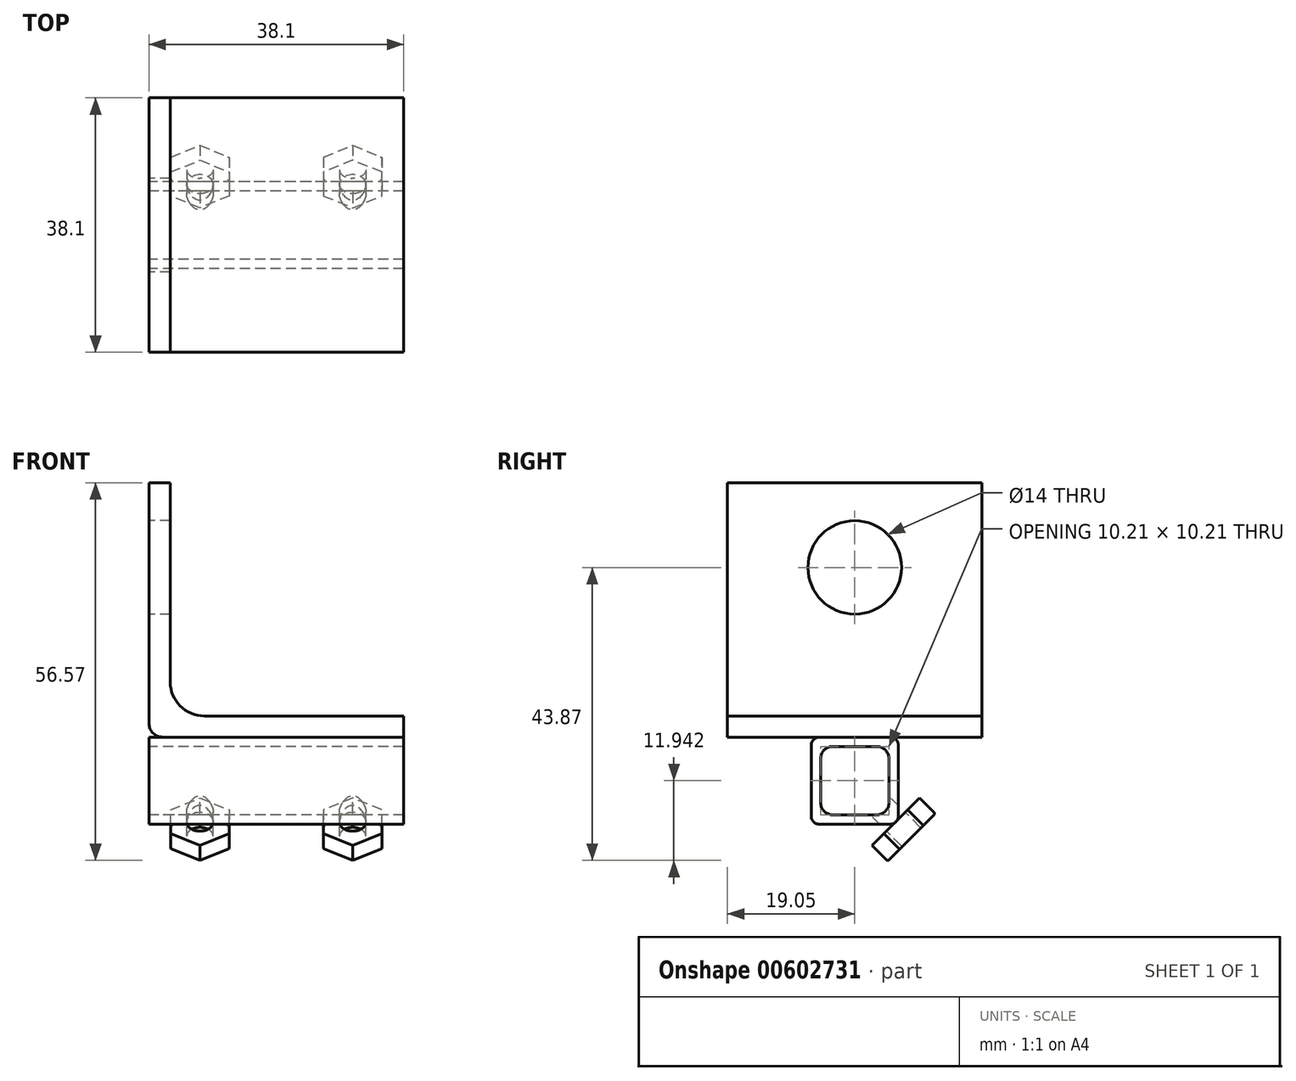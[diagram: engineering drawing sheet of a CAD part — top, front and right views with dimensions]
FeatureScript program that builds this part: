
annotation { "Feature Type Name" : "Feature", "Feature Type Description" : "" }
export const myFeature = defineFeature(function(context is Context, id is Id, definition is map)
    precondition{}
    {
        {
            var Q0;
            Q0=qCreatedBy(makeId("Front.planeOp"),FACE);
            var sketch = newSketch(context, id + "F0", { "sketchPlane" : qUnion([Q0])});
            skLineSegment(sketch, "E0", {"start": v(0, 38.1) * mm, "end": v(0, 0) * mm});
            skLineSegment(sketch, "E1", {"start": v(0, 0) * mm, "end": v(38.1, 0) * mm});
            skLineSegment(sketch, "E2", {"start": v(38.1, 0) * mm, "end": v(38.1, 3.17) * mm});
            skLineSegment(sketch, "E3", {"start": v(38.1, 3.17) * mm, "end": v(3.17, 3.17) * mm});
            skLineSegment(sketch, "E4", {"start": v(3.18, 3.17) * mm, "end": v(3.18, 38.1) * mm});
            skLineSegment(sketch, "E5", {"start": v(3.17, 38.1) * mm, "end": v(0, 38.1) * mm});
            skSolve(sketch);
        }
        {
            var Q0;
            Q0=makeQuery(id+"F0.imprint","IMPRINT",FACE,{"disambiguationData":[TD([[makeQuery(id+"F0.imprint","IMPRINT",EDGE,{"derivedFrom":sQuery(id+"F0.wireOp",EDGE,"E0")}),1.0]])]});
            extrude(context, id + "F1", {"entities" : qUnion([Q0]), "depth" : 38.1 * mm, "offsetDistance" : 25.4 * mm});
        }
        {
            var Q0;
            Q0=makeQuery(id+"F1.opExtrude","SWEPT_FACE",FACE,{"disambiguationData":[OSD([sQuery(id+"F0.wireOp",EDGE,"E0")])]});
            var sketch = newSketch(context, id + "F2", { "sketchPlane" : qUnion([Q0])});
            skCircle(sketch, "E6", {"center": v(19.05, 25.4) * mm, "radius": 7 * mm});
            skLineSegment(sketch, "E7", {"start": v(19.05, 38.1) * mm, "end": v(19.05, 25.4) * mm, "construction": true});
            skSolve(sketch);
        }
        {
            var Q0;
            Q0 = qSketchRegion(id + "F2", true);
            extrude(context, id + "F3", {"entities" : qUnion([Q0]), "operationType" : NewBodyOperationType.REMOVE, "endBound" : BoundingType.THROUGH_ALL, "oppositeDirection" : true, "depth" : 25.4 * mm, "offsetDistance" : 25.4 * mm});
        }
        {
            var Q0;
            Q0=makeQuery(id+"F1.opExtrude","SWEPT_EDGE",EDGE,{"disambiguationData":[OSD([sQuery(id+"F0.wireOp",EDGE,"E0"),sQuery(id+"F0.wireOp",EDGE,"E1")])]});
            fillet(context, id + "F4", {"entities" : qUnion([Q0]), "radius" : 2.03 * mm, "tangentPropagation" : true, "allowEdgeOverflow" : false});
        }
        {
            var Q0;
            Q0=makeQuery(id+"F1.opExtrude","SWEPT_EDGE",EDGE,{"disambiguationData":[OSD([sQuery(id+"F0.wireOp",EDGE,"E3"),sQuery(id+"F0.wireOp",EDGE,"E4")])]});
            fillet(context, id + "F5", {"entities" : qUnion([Q0]), "radius" : 5.08 * mm, "tangentPropagation" : true, "allowEdgeOverflow" : false});
        }
        {
            var Q0;
            Q0=makeQuery(id+"F1.opExtrude","SWEPT_FACE",FACE,{"disambiguationData":[OSD([sQuery(id+"F0.wireOp",EDGE,"E0")])]});
            var sketch = newSketch(context, id + "F6", { "sketchPlane" : qUnion([Q0])});
            skLineSegment(sketch, "E8.bottom", {"start": v(12.52, -13.06) * mm, "end": v(25.58, -13.06) * mm});
            skLineSegment(sketch, "E8.top", {"start": v(12.52, 0) * mm, "end": v(25.58, 0) * mm});
            skLineSegment(sketch, "E8.left", {"start": v(12.52, -13.06) * mm, "end": v(12.52, 0) * mm});
            skLineSegment(sketch, "E8.right", {"start": v(25.58, -13.06) * mm, "end": v(25.58, 0) * mm});
            skPoint(sketch, "E9", {"position": v(19.05, 0) * mm});
            skSolve(sketch);
        }
        {
            var Q0;
            Q0 = qSketchRegion(id + "F6", true);
            var Q1;
            Q1=makeQuery(id+"F1.opExtrude","SWEPT_FACE",FACE,{"disambiguationData":[OSD([sQuery(id+"F0.wireOp",EDGE,"E2")])]});
            extrude(context, id + "F7", {"entities" : qUnion([Q0]), "endBound" : BoundingType.UP_TO_SURFACE, "oppositeDirection" : true, "depth" : 25.4 * mm, "endBoundEntityFace" : qUnion([Q1]), "offsetDistance" : 25.4 * mm});
        }
        {
            var Q0;
            Q0=makeQuery(id+"F7.opExtrude","CAP_FACE",FACE,{"disambiguationData":[OSD([sQuery(id+"F6.wireOp",EDGE,"E8.bottom"),sQuery(id+"F6.wireOp",EDGE,"E8.top"),sQuery(id+"F6.wireOp",EDGE,"E8.left"),sQuery(id+"F6.wireOp",EDGE,"E8.right")])],"isStart":false});
            var Q1;
            Q1=makeQuery(id+"F7.opExtrude","CAP_FACE",FACE,{"disambiguationData":[OSD([sQuery(id+"F6.wireOp",EDGE,"E8.bottom"),sQuery(id+"F6.wireOp",EDGE,"E8.top"),sQuery(id+"F6.wireOp",EDGE,"E8.left"),sQuery(id+"F6.wireOp",EDGE,"E8.right")])],"isStart":true});
            shell(context, id + "F8", {"entities" : qUnion([Q0, Q1]), "thickness" : 1.42 * mm});
        }
        {
            var Q0;
            Q0=makeQuery(id+"F7.opExtrude","SWEPT_EDGE",EDGE,{"disambiguationData":[OSD([sQuery(id+"F6.wireOp",EDGE,"E8.bottom"),sQuery(id+"F6.wireOp",EDGE,"E8.right")])]});
            var Q1;
            Q1=makeQuery(id+"F7.opExtrude","SWEPT_EDGE",EDGE,{"disambiguationData":[OSD([sQuery(id+"F6.wireOp",EDGE,"E8.top"),sQuery(id+"F6.wireOp",EDGE,"E8.right")])]});
            var Q2;
            Q2=makeQuery(id+"F7.opExtrude","SWEPT_EDGE",EDGE,{"disambiguationData":[OSD([sQuery(id+"F6.wireOp",EDGE,"E8.bottom"),sQuery(id+"F6.wireOp",EDGE,"E8.left")])]});
            var Q3;
            Q3=makeQuery(id+"F7.opExtrude","SWEPT_EDGE",EDGE,{"disambiguationData":[OSD([sQuery(id+"F6.wireOp",EDGE,"E8.top"),sQuery(id+"F6.wireOp",EDGE,"E8.left")])]});
            fillet(context, id + "F9", {"entities" : qUnion([Q0, Q1, Q2, Q3]), "radius" : 1.27 * mm, "tangentPropagation" : true, "allowEdgeOverflow" : false});
        }
        {
            var Q0;
            Q0=makeQuery(id+"F8.opShell","OFFSET_EDGE",EDGE,{"disambiguationData":[OSD([sQuery(id+"F6.wireOp",EDGE,"E8.bottom"),sQuery(id+"F6.wireOp",EDGE,"E8.right")])]});
            var Q1;
            Q1=makeQuery(id+"F8.opShell","OFFSET_EDGE",EDGE,{"disambiguationData":[OSD([sQuery(id+"F6.wireOp",EDGE,"E8.top"),sQuery(id+"F6.wireOp",EDGE,"E8.right")])]});
            var Q2;
            Q2=makeQuery(id+"F8.opShell","OFFSET_EDGE",EDGE,{"disambiguationData":[OSD([sQuery(id+"F6.wireOp",EDGE,"E8.top"),sQuery(id+"F6.wireOp",EDGE,"E8.left")])]});
            var Q3;
            Q3=makeQuery(id+"F8.opShell","OFFSET_EDGE",EDGE,{"disambiguationData":[OSD([sQuery(id+"F6.wireOp",EDGE,"E8.bottom"),sQuery(id+"F6.wireOp",EDGE,"E8.left")])]});
            fillet(context, id + "F10", {"entities" : qUnion([Q0, Q1, Q2, Q3]), "radius" : 1.78 * mm, "tangentPropagation" : true, "allowEdgeOverflow" : false});
        }
        {
            var Q0;
            Q0=makeQuery(id+"F7.opExtrude","SWEPT_FACE",FACE,{"disambiguationData":[OSD([sQuery(id+"F6.wireOp",EDGE,"E8.bottom")])]});
            var Q1;
            {var subQ0=sQuery(id+"F6.wireOp",EDGE,"E8.bottom");Q1=makeQuery(id+"F9.opFillet","BLEND_EDGE",EDGE,{"blendedFrom":[makeQuery(id+"F7.opExtrude","SWEPT_EDGE",EDGE,{"disambiguationData":[OSD([subQ0,sQuery(id+"F6.wireOp",EDGE,"E8.right")])]}),makeQuery(id+"F7.opExtrude","SWEPT_FACE",FACE,{"disambiguationData":[OSD([subQ0])]})],"blendedInto":[makeQuery(id+"F7.opExtrude","SWEPT_FACE",FACE,{"disambiguationData":[OSD([subQ0])]})]});}
            cPlane(context, id + "F11", {"entities" : qUnion([Q0, Q1]), "cplaneType" : CPlaneType.LINE_ANGLE, "offset" : 25.4 * mm, "angle" : 45 * degree, "oppositeDirection" : true, "width" : 152.4 * mm, "height" : 152.4 * mm});
        }
        {
            var Q0;
            Q0=qCreatedBy(id+"F11.planeOp",FACE);
            var sketch = newSketch(context, id + "F12", { "sketchPlane" : qUnion([Q0])});
            skCircle(sketch, "E10", {"center": v(30.48, -18.09) * mm, "radius": 1.98 * mm});
            skLineSegment(sketch, "E11", {"start": v(30.48, -18.09) * mm, "end": v(38.1, -18.09) * mm, "construction": true});
            skLineSegment(sketch, "E12", {"start": v(19.05, -18.98) * mm, "end": v(19.05, -28.6) * mm, "construction": true});
            skCircle(sketch, "E13.MirrorC", {"center": v(7.62, -18.09) * mm, "radius": 1.98 * mm});
            skSolve(sketch);
        }
        {
            var Q0;
            Q0 = qSketchRegion(id + "F12", true);
            extrude(context, id + "F13", {"entities" : qUnion([Q0]), "operationType" : NewBodyOperationType.REMOVE, "endBound" : BoundingType.THROUGH_ALL, "oppositeDirection" : true, "depth" : 25.4 * mm, "offsetDistance" : 25.4 * mm});
        }
        {
            var Q0;
            {var subQ0=sQuery(id+"F6.wireOp",EDGE,"E8.left");var subQ1=sQuery(id+"F6.wireOp",EDGE,"E8.bottom");Q0=makeQuery(id+"F9.opFillet","BLEND_EDGE",EDGE,{"blendedFrom":[makeQuery(id+"F7.opExtrude","SWEPT_EDGE",EDGE,{"disambiguationData":[OSD([subQ1,subQ0])]}),makeQuery(id+"F7.opExtrude","CAP_FACE",FACE,{"disambiguationData":[OSD([subQ1,sQuery(id+"F6.wireOp",EDGE,"E8.top"),subQ0,sQuery(id+"F6.wireOp",EDGE,"E8.right")])],"isStart":true})],"blendedInto":[makeQuery(id+"F7.opExtrude","CAP_FACE",FACE,{"disambiguationData":[OSD([subQ1,sQuery(id+"F6.wireOp",EDGE,"E8.top"),subQ0,sQuery(id+"F6.wireOp",EDGE,"E8.right")])],"isStart":true})]});}
            cPoint(context, id + "F14", {"entities" : qUnion([Q0]), "parameter" : 0.5});
        }
        {
            var Q0;
            Q0 = qCreatedBy(id + "F14" ,VERTEX);
            var Q1;
            Q1=qCreatedBy(id+"F11.planeOp",FACE);
            cPlane(context, id + "F15", {"entities" : qUnion([Q0, Q1]), "cplaneType" : CPlaneType.PLANE_POINT, "offset" : 25.4 * mm, "width" : 152.4 * mm, "height" : 152.4 * mm});
        }
        {
            var Q0;
            Q0=qCreatedBy(id+"F15.planeOp",FACE);
            var sketch = newSketch(context, id + "F16", { "sketchPlane" : qUnion([Q0])});
            skCircle(sketch, "E14.cCircle", {"center": v(7.62, -18.09) * mm, "radius": 4.37 * mm, "construction": true});
            skLineSegment(sketch, "E14.0", {"start": v(11.99, -15.57) * mm, "end": v(11.99, -20.6) * mm});
            skLineSegment(sketch, "E14.1", {"start": v(11.99, -20.6) * mm, "end": v(7.62, -23.13) * mm});
            skLineSegment(sketch, "E14.2", {"start": v(7.62, -23.13) * mm, "end": v(3.25, -20.6) * mm});
            skLineSegment(sketch, "E14.3", {"start": v(3.25, -20.6) * mm, "end": v(3.25, -15.57) * mm});
            skLineSegment(sketch, "E14.4", {"start": v(3.25, -15.57) * mm, "end": v(7.62, -13.05) * mm});
            skLineSegment(sketch, "E14.5", {"start": v(7.62, -13.05) * mm, "end": v(11.99, -15.57) * mm});
            skPoint(sketch, "E14.0.midPoint", {"position": v(11.99, -18.09) * mm});
            skCircle(sketch, "E15", {"center": v(7.62, -18.09) * mm, "radius": 1.98 * mm});
            skLineSegment(sketch, "E16", {"start": v(19.05, -29.78) * mm, "end": v(19.05, -18.98) * mm, "construction": true});
            skLineSegment(sketch, "E17.MirrorCS", {"start": v(30.48, -13.05) * mm, "end": v(26.11, -15.57) * mm});
            skLineSegment(sketch, "E18.MirrorCS", {"start": v(34.85, -15.57) * mm, "end": v(30.48, -13.05) * mm});
            skLineSegment(sketch, "E19.MirrorCS", {"start": v(34.85, -20.6) * mm, "end": v(34.85, -15.57) * mm});
            skLineSegment(sketch, "E20.MirrorCS", {"start": v(30.48, -23.13) * mm, "end": v(34.85, -20.6) * mm});
            skLineSegment(sketch, "E21.MirrorCS", {"start": v(26.11, -20.6) * mm, "end": v(30.48, -23.13) * mm});
            skLineSegment(sketch, "E22.MirrorCS", {"start": v(26.11, -15.57) * mm, "end": v(26.11, -20.6) * mm});
            skCircle(sketch, "E23.MirrorC", {"center": v(30.48, -18.09) * mm, "radius": 1.98 * mm});
            skSolve(sketch);
        }
        {
            var Q0;
            Q0 = qSketchRegion(id + "F16", true);
            extrude(context, id + "F17", {"entities" : qUnion([Q0]), "oppositeDirection" : true, "depth" : 3.3 * mm, "offsetDistance" : 25.4 * mm});
        }
        {
            var Q0;
            Q0=makeQuery(id+"F17.opExtrude","CAP_FACE",FACE,{"disambiguationData":[OSD([sQuery(id+"F16.wireOp",EDGE,"E17.MirrorCS"),sQuery(id+"F16.wireOp",EDGE,"E18.MirrorCS"),sQuery(id+"F16.wireOp",EDGE,"E19.MirrorCS"),sQuery(id+"F16.wireOp",EDGE,"E20.MirrorCS"),sQuery(id+"F16.wireOp",EDGE,"E21.MirrorCS"),sQuery(id+"F16.wireOp",EDGE,"E22.MirrorCS"),sQuery(id+"F16.wireOp",EDGE,"E23.MirrorC")])],"isStart":false});
            var Q1;
            Q1=makeQuery(id+"F17.opExtrude","CAP_FACE",FACE,{"disambiguationData":[OSD([sQuery(id+"F16.wireOp",EDGE,"E14.0"),sQuery(id+"F16.wireOp",EDGE,"E14.1"),sQuery(id+"F16.wireOp",EDGE,"E14.2"),sQuery(id+"F16.wireOp",EDGE,"E14.3"),sQuery(id+"F16.wireOp",EDGE,"E14.4"),sQuery(id+"F16.wireOp",EDGE,"E14.5"),sQuery(id+"F16.wireOp",EDGE,"E15")])],"isStart":false});
            fillet(context, id + "F18", {"entities" : qUnion([Q0, Q1]), "radius" : 0.25 * mm, "tangentPropagation" : true, "allowEdgeOverflow" : false});
        }
    });
